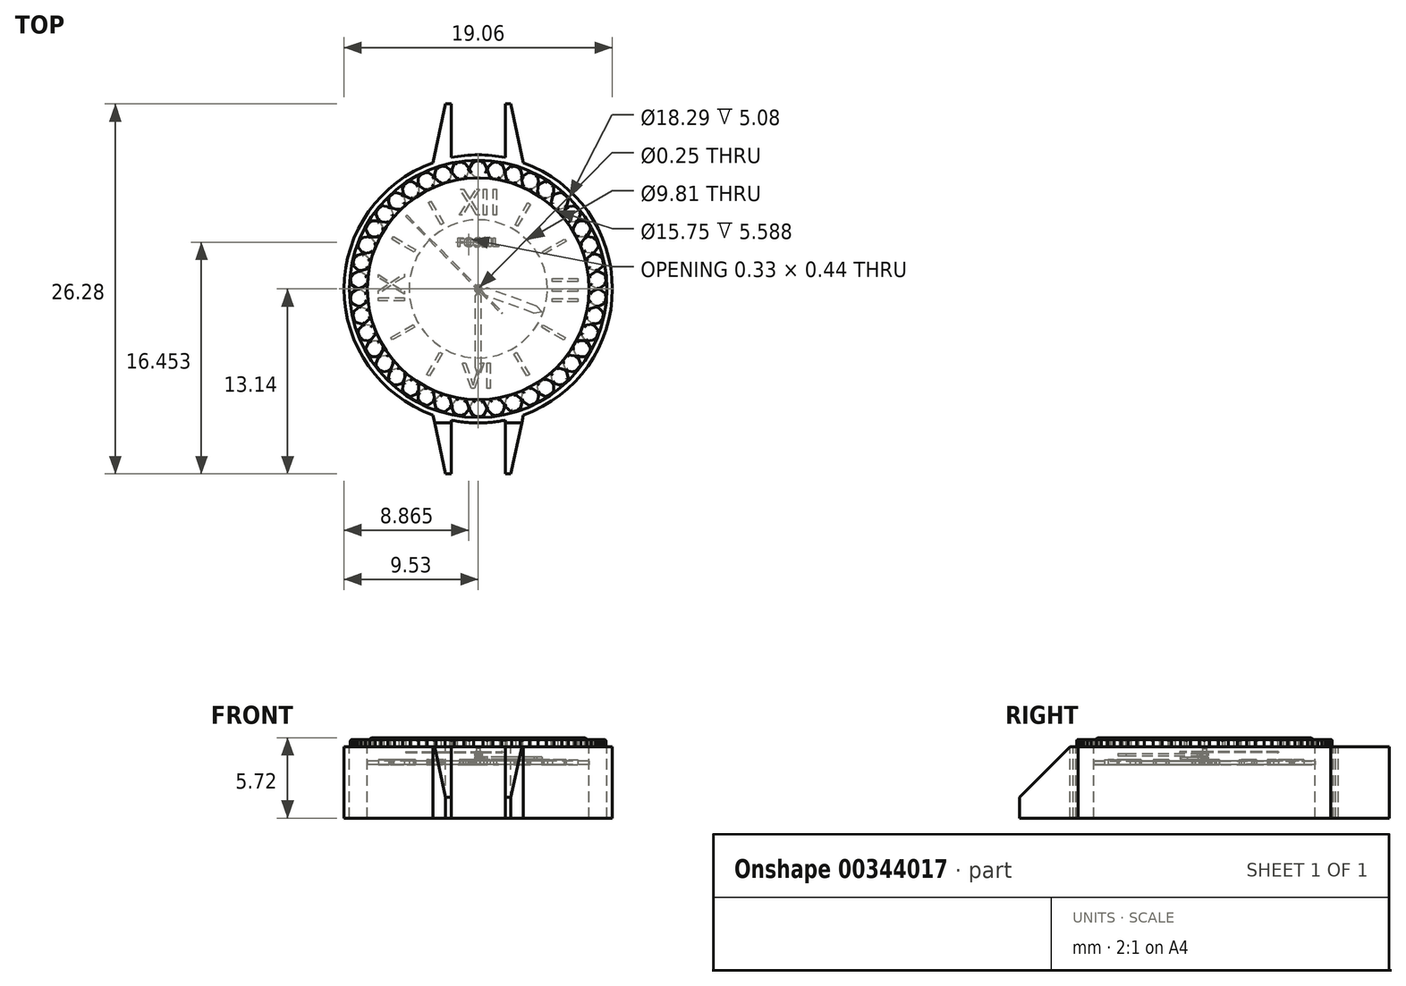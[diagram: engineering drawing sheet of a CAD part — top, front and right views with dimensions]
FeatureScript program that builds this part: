
annotation { "Feature Type Name" : "Feature", "Feature Type Description" : "" }
export const myFeature = defineFeature(function(context is Context, id is Id, definition is map)
    precondition{}
    {
        {
            var Q0;
            Q0=qCreatedBy(makeId("Top.planeOp"),FACE);
            var sketch = newSketch(context, id + "F0", { "sketchPlane" : qUnion([Q0])});
            skCircle(sketch, "E0", {"center": v(0, 0) * mm, "radius": 7.87 * mm});
            skCircle(sketch, "E1", {"center": v(0, 0) * mm, "radius": 9.14 * mm});
            skArc(sketch, "E2", {"start": v(1.93, 9.33) * mm, "mid": v(0, 9.53) * mm, "end": v(-1.93, 9.33) * mm});
            skLineSegment(sketch, "E3", {"start": v(3.22, 8.97) * mm, "end": v(2.32, 13.14) * mm});
            skLineSegment(sketch, "E4", {"start": v(1.93, 13.14) * mm, "end": v(1.93, 9.33) * mm});
            skLineSegment(sketch, "E5.MirrorCS", {"start": v(1.93, -13.14) * mm, "end": v(1.93, -9.33) * mm});
            skLineSegment(sketch, "E6.MirrorCS", {"start": v(3.22, -8.97) * mm, "end": v(2.32, -13.14) * mm});
            skLineSegment(sketch, "E7.MirrorCS", {"start": v(-1.93, 13.14) * mm, "end": v(-1.93, 9.33) * mm});
            skLineSegment(sketch, "E8.MirrorCS", {"start": v(-3.22, 8.97) * mm, "end": v(-2.32, 13.14) * mm});
            skLineSegment(sketch, "E9.MirrorCS", {"start": v(-3.22, -8.97) * mm, "end": v(-2.32, -13.14) * mm});
            skLineSegment(sketch, "E10.MirrorCS", {"start": v(-1.93, -13.14) * mm, "end": v(-1.93, -9.33) * mm});
            skArc(sketch, "E11.trimOffspring", {"start": v(-3.22, 8.97) * mm, "mid": v(-9.52, 0) * mm, "end": v(-3.22, -8.97) * mm});
            skArc(sketch, "E12.trimOffspring", {"start": v(3.22, -8.97) * mm, "mid": v(9.53, 0) * mm, "end": v(3.22, 8.97) * mm});
            skArc(sketch, "E13.trimOffspring", {"start": v(-1.93, -9.33) * mm, "mid": v(0, -9.53) * mm, "end": v(1.93, -9.33) * mm});
            skLineSegment(sketch, "E14", {"start": v(2.32, 13.14) * mm, "end": v(1.93, 13.14) * mm});
            skLineSegment(sketch, "E15.MirrorCS", {"start": v(-2.32, 13.14) * mm, "end": v(-1.93, 13.14) * mm});
            skLineSegment(sketch, "E16.MirrorCS", {"start": v(2.32, -13.14) * mm, "end": v(1.93, -13.14) * mm});
            skLineSegment(sketch, "E17.MirrorCS", {"start": v(-2.32, -13.14) * mm, "end": v(-1.93, -13.14) * mm});
            skLineSegment(sketch, "E18", {"start": v(0, 7.87) * mm, "end": v(0, -7.87) * mm, "construction": true});
            skSolve(sketch);
        }
        {
            var Q0;
            Q0=makeQuery(id+"F0.imprint","IMPRINT",FACE,{"disambiguationData":[TD([[makeQuery(id+"F0.imprint","IMPRINT",EDGE,{"derivedFrom":sQuery(id+"F0.wireOp",EDGE,"E1")}),-1.0]])]});
            var Q1;
            Q1=sQuery(id+"F0.wireOp",EDGE,"E12.trimOffspring");
            var Q2;
            Q2=sQuery(id+"F0.wireOp",EDGE,"E6.MirrorCS");
            var Q3;
            Q3=sQuery(id+"F0.wireOp",EDGE,"E5.MirrorCS");
            var Q4;
            Q4=sQuery(id+"F0.wireOp",EDGE,"E13.trimOffspring");
            var Q5;
            Q5=sQuery(id+"F0.wireOp",EDGE,"E10.MirrorCS");
            var Q6;
            Q6=sQuery(id+"F0.wireOp",EDGE,"E17.MirrorCS");
            var Q7;
            Q7=sQuery(id+"F0.wireOp",EDGE,"E9.MirrorCS");
            var Q8;
            Q8=sQuery(id+"F0.wireOp",EDGE,"E11.trimOffspring");
            extrude(context, id + "F1", {"entities" : qUnion([Q0]), "surfaceEntities" : qUnion([Q1, Q2, Q3, Q4, Q5, Q6, Q7, Q8]), "oppositeDirection" : true, "depth" : 5.08 * mm});
        }
        {
            var Q0;
            Q0=qCreatedBy(makeId("Top.planeOp"),FACE);
            cPlane(context, id + "F2", {"entities" : qUnion([Q0]), "cplaneType" : CPlaneType.OFFSET, "offset" : 1.27 * mm, "oppositeDirection" : true, "width" : 152.4 * mm, "height" : 152.4 * mm});
        }
        {
            var Q0;
            Q0=qCreatedBy(id+"F2.planeOp",FACE);
            var sketch = newSketch(context, id + "F3", { "sketchPlane" : qUnion([Q0])});
            skCircle(sketch, "E19", {"center": v(0.05, 0) * mm, "radius": 7.87 * mm, "construction": true});
            skLineSegment(sketch, "E20", {"start": v(0.05, 7.09) * mm, "end": v(0.05, 0) * mm, "construction": true});
            skText(sketch, "E21", { "text": "XII", "fontName": "OpenSans-Regular.ttf"});
            skLineSegment(sketch, "E22.1.0", {"start": v(-3.5, 6.16) * mm, "end": v(0.05, 0.03) * mm, "construction": true});
            skLineSegment(sketch, "E22.2.0", {"start": v(-6.1, 3.59) * mm, "end": v(0.03, 0.05) * mm, "construction": true});
            skLineSegment(sketch, "E22.3.0", {"start": v(-7.09, 0.05) * mm, "end": v(0, 0.05) * mm, "construction": true});
            skLineSegment(sketch, "E22.4.0", {"start": v(-6.16, -3.5) * mm, "end": v(-0.03, 0.05) * mm, "construction": true});
            skLineSegment(sketch, "E22.5.0", {"start": v(-3.59, -6.1) * mm, "end": v(-0.05, 0.03) * mm, "construction": true});
            skLineSegment(sketch, "E22.6.0", {"start": v(-0.05, -7.09) * mm, "end": v(-0.05, 0) * mm, "construction": true});
            skLineSegment(sketch, "E22.7.0", {"start": v(3.5, -6.16) * mm, "end": v(-0.05, -0.03) * mm, "construction": true});
            skLineSegment(sketch, "E22.8.0", {"start": v(6.1, -3.59) * mm, "end": v(-0.03, -0.05) * mm, "construction": true});
            skLineSegment(sketch, "E22.9.0", {"start": v(7.09, -0.05) * mm, "end": v(0, -0.05) * mm, "construction": true});
            skLineSegment(sketch, "E22.10.0", {"start": v(6.16, 3.5) * mm, "end": v(0.03, -0.05) * mm, "construction": true});
            skLineSegment(sketch, "E22.11.0", {"start": v(3.59, 6.1) * mm, "end": v(0.05, -0.03) * mm, "construction": true});
            skPoint(sketch, "E22.center", {"position": v(0, 0) * mm});
            skText(sketch, "E23", { "text": "I", "fontName": "OpenSans-Regular.ttf"});
            skText(sketch, "E24", { "text": "III", "fontName": "OpenSans-Regular.ttf"});
            skText(sketch, "E25", { "text": "I", "fontName": "OpenSans-Regular.ttf"});
            skText(sketch, "E26", { "text": "I", "fontName": "OpenSans-Regular.ttf"});
            skText(sketch, "E27", { "text": "I", "fontName": "OpenSans-Regular.ttf"});
            skText(sketch, "E28", { "text": "VI", "fontName": "OpenSans-Regular.ttf"});
            skText(sketch, "E29", { "text": "I", "fontName": "OpenSans-Regular.ttf"});
            skText(sketch, "E30", { "text": "I", "fontName": "OpenSans-Regular.ttf"});
            skText(sketch, "E31", { "text": "IX", "fontName": "OpenSans-Regular.ttf"});
            skText(sketch, "E32", { "text": "I", "fontName": "OpenSans-Regular.ttf"});
            skText(sketch, "E33", { "text": "I", "fontName": "OpenSans-Regular.ttf"});
            skPoint(sketch, "E33.secondSnap0", {"position": v(-1.67, 5.13) * mm});
            const initialGuessF3  = {"E21": [-0.00134, 0.00526, 1, 0, 0.00183], "E23": [0.0024, 0.00468, 0.86603, -0.5, 0.00183], "E24": [0.00526, 0.00097, 0, -1, 0.00183], "E25": [0.00443, 0.00285, 0.5, -0.86603, 0.00183], "E26": [0.00595, -0.00386, 0.5, 0.86603, 0.00183], "E27": [0.00323, -0.00632, 0.86603, 0.5, 0.00183], "E28": [-0.00112, -0.00709, 1, 0, 0.00183], "E29": [-0.00386, -0.00595, 0.86603, -0.5, 0.00183], "E30": [-0.00632, -0.00323, 0.5, -0.86603, 0.00183], "E31": [-0.00526, -0.0011, 0, 1, 0.00183], "E32": [-0.00468, 0.0024, 0.5, 0.86603, 0.00183], "E33": [-0.00285, 0.00443, 0.86603, 0.5, 0.00183]};
            skSetInitialGuess(sketch, initialGuessF3);
            skSolve(sketch);
        }
        {
            var Q0;
            Q0=qCreatedBy(makeId("Front.planeOp"),FACE);
            var sketch = newSketch(context, id + "F4", { "sketchPlane" : qUnion([Q0])});
            skLineSegment(sketch, "E34", {"start": v(0, 57.98) * mm, "end": v(0, -59.61) * mm, "construction": true});
            skSolve(sketch);
        }
        {
            var Q0;
            Q0 = qSketchRegion(id + "F3", true);
            extrude(context, id + "F5", {"entities" : qUnion([Q0]), "depth" : 0.33 * mm});
        }
        {
            var Q0;
            Q0=makeQuery(id+"F0.imprint","IMPRINT",FACE,{"disambiguationData":[TD([[makeQuery(id+"F0.imprint","IMPRINT",EDGE,{"derivedFrom":sQuery(id+"F0.wireOp",EDGE,"E0")}),1.0]])]});
            var Q1;
            Q1=sQuery(id+"F0.wireOp",EDGE,"E18");
            var Q2;
            Q2=sQuery(id+"F0.wireOp",EDGE,"E0");
            extrude(context, id + "F6", {"entities" : qUnion([Q0]), "surfaceEntities" : qUnion([Q1, Q2]), "depth" : 0.64 * mm});
        }
        {
            var Q0;
            Q0=makeQuery(id+"F6.opExtrude","CAP_FACE",FACE,{"disambiguationData":[OSD([sQuery(id+"F0.wireOp",EDGE,"E0")])],"isStart":false});
            fillet(context, id + "F7", {"entities" : qUnion([Q0]), "radius" : 0.43 * mm, "tangentPropagation" : true, "allowEdgeOverflow" : false});
        }
        {
            var Q0;
            Q0=makeQuery(id+"F0.imprint","IMPRINT",FACE,{"disambiguationData":[TD([[makeQuery(id+"F0.imprint","IMPRINT",EDGE,{"derivedFrom":sQuery(id+"F0.wireOp",EDGE,"E0")}),-1.0]])]});
            var Q1;
            Q1=makeQuery(id+"F1.opExtrude","CAP_FACE",FACE,{"disambiguationData":[OSD([sQuery(id+"F0.wireOp",EDGE,"E1"),sQuery(id+"F0.wireOp",EDGE,"E2"),sQuery(id+"F0.wireOp",EDGE,"E3"),sQuery(id+"F0.wireOp",EDGE,"E4"),sQuery(id+"F0.wireOp",EDGE,"E5.MirrorCS"),sQuery(id+"F0.wireOp",EDGE,"E6.MirrorCS"),sQuery(id+"F0.wireOp",EDGE,"E7.MirrorCS"),sQuery(id+"F0.wireOp",EDGE,"E8.MirrorCS"),sQuery(id+"F0.wireOp",EDGE,"E9.MirrorCS"),sQuery(id+"F0.wireOp",EDGE,"E10.MirrorCS"),sQuery(id+"F0.wireOp",EDGE,"E11.trimOffspring"),sQuery(id+"F0.wireOp",EDGE,"E12.trimOffspring"),sQuery(id+"F0.wireOp",EDGE,"E13.trimOffspring"),sQuery(id+"F0.wireOp",EDGE,"E14"),sQuery(id+"F0.wireOp",EDGE,"E15.MirrorCS"),sQuery(id+"F0.wireOp",EDGE,"E16.MirrorCS"),sQuery(id+"F0.wireOp",EDGE,"E17.MirrorCS")])],"isStart":false});
            extrude(context, id + "F8", {"entities" : qUnion([Q0]), "endBound" : BoundingType.UP_TO_SURFACE, "oppositeDirection" : true, "endBoundEntityFace" : qUnion([Q1]), "depth" : 25.4 * mm, "hasSecondDirection" : true, "secondDirectionOppositeDirection" : false, "secondDirectionDepth" : 0.5 * mm});
        }
        {
            var Q0;
            Q0=makeQuery(id+"F0.imprint","IMPRINT",FACE,{"disambiguationData":[TD([[makeQuery(id+"F0.imprint","IMPRINT",EDGE,{"derivedFrom":sQuery(id+"F0.wireOp",EDGE,"E0")}),-1.0]])]});
            var sketch = newSketch(context, id + "F9", { "sketchPlane" : qUnion([Q0])});
            skCircle(sketch, "E35.cCircle", {"center": v(0, 8.5) * mm, "radius": 0.57 * mm});
            skLineSegment(sketch, "E35.0", {"start": v(0.65, 8.5) * mm, "end": v(0.33, 7.94) * mm});
            skLineSegment(sketch, "E35.1", {"start": v(0.33, 7.94) * mm, "end": v(-0.33, 7.94) * mm});
            skLineSegment(sketch, "E35.2", {"start": v(-0.33, 7.94) * mm, "end": v(-0.65, 8.5) * mm});
            skLineSegment(sketch, "E35.3", {"start": v(-0.65, 8.5) * mm, "end": v(-0.33, 9.08) * mm});
            skLineSegment(sketch, "E35.4", {"start": v(-0.33, 9.08) * mm, "end": v(0.33, 9.08) * mm});
            skLineSegment(sketch, "E35.5", {"start": v(0.33, 9.08) * mm, "end": v(0.65, 8.5) * mm});
            skPoint(sketch, "E35.0.midPoint", {"position": v(0.5, 8.23) * mm});
            skPoint(sketch, "E36.center", {"position": v(0, 0) * mm});
            skLineSegment(sketch, "E37.1.0", {"start": v(-1.68, 8.93) * mm, "end": v(-1.03, 9.02) * mm});
            skLineSegment(sketch, "E37.1.1", {"start": v(-1.03, 9.02) * mm, "end": v(-0.62, 8.51) * mm});
            skLineSegment(sketch, "E37.1.2", {"start": v(-0.62, 8.51) * mm, "end": v(-0.86, 7.9) * mm});
            skLineSegment(sketch, "E37.1.3", {"start": v(-0.86, 7.9) * mm, "end": v(-1.5, 7.8) * mm});
            skLineSegment(sketch, "E37.1.4", {"start": v(-1.5, 7.8) * mm, "end": v(-1.91, 8.32) * mm});
            skLineSegment(sketch, "E37.1.5", {"start": v(-1.91, 8.32) * mm, "end": v(-1.68, 8.93) * mm});
            skLineSegment(sketch, "E37.2.0", {"start": v(-2.99, 8.58) * mm, "end": v(-2.36, 8.77) * mm});
            skLineSegment(sketch, "E37.2.1", {"start": v(-2.36, 8.77) * mm, "end": v(-1.88, 8.32) * mm});
            skLineSegment(sketch, "E37.2.2", {"start": v(-1.88, 8.32) * mm, "end": v(-2.03, 7.69) * mm});
            skLineSegment(sketch, "E37.2.3", {"start": v(-2.03, 7.69) * mm, "end": v(-2.65, 7.5) * mm});
            skLineSegment(sketch, "E37.2.4", {"start": v(-2.65, 7.5) * mm, "end": v(-3.13, 7.94) * mm});
            skLineSegment(sketch, "E37.2.5", {"start": v(-3.13, 7.94) * mm, "end": v(-2.99, 8.58) * mm});
            skLineSegment(sketch, "E37.3.0", {"start": v(-4.23, 8.03) * mm, "end": v(-3.64, 8.32) * mm});
            skLineSegment(sketch, "E37.3.1", {"start": v(-3.64, 8.32) * mm, "end": v(-3.1, 7.95) * mm});
            skLineSegment(sketch, "E37.3.2", {"start": v(-3.1, 7.95) * mm, "end": v(-3.15, 7.3) * mm});
            skLineSegment(sketch, "E37.3.3", {"start": v(-3.15, 7.3) * mm, "end": v(-3.74, 7.01) * mm});
            skLineSegment(sketch, "E37.3.4", {"start": v(-3.74, 7.01) * mm, "end": v(-4.28, 7.38) * mm});
            skLineSegment(sketch, "E37.3.5", {"start": v(-4.28, 7.38) * mm, "end": v(-4.23, 8.03) * mm});
            skLineSegment(sketch, "E37.4.0", {"start": v(-5.38, 7.31) * mm, "end": v(-4.84, 7.68) * mm});
            skLineSegment(sketch, "E37.4.1", {"start": v(-4.84, 7.68) * mm, "end": v(-4.25, 7.4) * mm});
            skLineSegment(sketch, "E37.4.2", {"start": v(-4.25, 7.4) * mm, "end": v(-4.2, 6.75) * mm});
            skLineSegment(sketch, "E37.4.3", {"start": v(-4.2, 6.75) * mm, "end": v(-4.74, 6.38) * mm});
            skLineSegment(sketch, "E37.4.4", {"start": v(-4.74, 6.38) * mm, "end": v(-5.33, 6.66) * mm});
            skLineSegment(sketch, "E37.4.5", {"start": v(-5.33, 6.66) * mm, "end": v(-5.38, 7.31) * mm});
            skLineSegment(sketch, "E37.5.0", {"start": v(-6.41, 6.43) * mm, "end": v(-5.93, 6.88) * mm});
            skLineSegment(sketch, "E37.5.1", {"start": v(-5.93, 6.88) * mm, "end": v(-5.3, 6.68) * mm});
            skLineSegment(sketch, "E37.5.2", {"start": v(-5.3, 6.68) * mm, "end": v(-5.16, 6.04) * mm});
            skLineSegment(sketch, "E37.5.3", {"start": v(-5.16, 6.04) * mm, "end": v(-5.64, 5.6) * mm});
            skLineSegment(sketch, "E37.5.4", {"start": v(-5.64, 5.6) * mm, "end": v(-6.27, 5.8) * mm});
            skLineSegment(sketch, "E37.5.5", {"start": v(-6.27, 5.8) * mm, "end": v(-6.41, 6.43) * mm});
            skLineSegment(sketch, "E37.6.0", {"start": v(-7.3, 5.4) * mm, "end": v(-6.9, 5.91) * mm});
            skLineSegment(sketch, "E37.6.1", {"start": v(-6.9, 5.91) * mm, "end": v(-6.24, 5.82) * mm});
            skLineSegment(sketch, "E37.6.2", {"start": v(-6.24, 5.82) * mm, "end": v(-6, 5.2) * mm});
            skLineSegment(sketch, "E37.6.3", {"start": v(-6, 5.2) * mm, "end": v(-6.41, 4.7) * mm});
            skLineSegment(sketch, "E37.6.4", {"start": v(-6.41, 4.7) * mm, "end": v(-7.06, 4.8) * mm});
            skLineSegment(sketch, "E37.6.5", {"start": v(-7.06, 4.8) * mm, "end": v(-7.3, 5.4) * mm});
            skLineSegment(sketch, "E37.7.0", {"start": v(-8.02, 4.25) * mm, "end": v(-7.7, 4.82) * mm});
            skLineSegment(sketch, "E37.7.1", {"start": v(-7.7, 4.82) * mm, "end": v(-7.04, 4.82) * mm});
            skLineSegment(sketch, "E37.7.2", {"start": v(-7.04, 4.82) * mm, "end": v(-6.71, 4.25) * mm});
            skLineSegment(sketch, "E37.7.3", {"start": v(-6.71, 4.25) * mm, "end": v(-7.04, 3.69) * mm});
            skLineSegment(sketch, "E37.7.4", {"start": v(-7.04, 3.69) * mm, "end": v(-7.7, 3.69) * mm});
            skLineSegment(sketch, "E37.7.5", {"start": v(-7.7, 3.69) * mm, "end": v(-8.02, 4.25) * mm});
            skLineSegment(sketch, "E37.8.0", {"start": v(-8.57, 3.01) * mm, "end": v(-8.33, 3.62) * mm});
            skLineSegment(sketch, "E37.8.1", {"start": v(-8.33, 3.62) * mm, "end": v(-7.68, 3.72) * mm});
            skLineSegment(sketch, "E37.8.2", {"start": v(-7.68, 3.72) * mm, "end": v(-7.27, 3.2) * mm});
            skLineSegment(sketch, "E37.8.3", {"start": v(-7.27, 3.2) * mm, "end": v(-7.51, 2.6) * mm});
            skLineSegment(sketch, "E37.8.4", {"start": v(-7.51, 2.6) * mm, "end": v(-8.16, 2.5) * mm});
            skLineSegment(sketch, "E37.8.5", {"start": v(-8.16, 2.5) * mm, "end": v(-8.57, 3.01) * mm});
            skLineSegment(sketch, "E37.9.0", {"start": v(-8.92, 1.7) * mm, "end": v(-8.77, 2.34) * mm});
            skLineSegment(sketch, "E37.9.1", {"start": v(-8.77, 2.34) * mm, "end": v(-8.15, 2.53) * mm});
            skLineSegment(sketch, "E37.9.2", {"start": v(-8.15, 2.53) * mm, "end": v(-7.67, 2.09) * mm});
            skLineSegment(sketch, "E37.9.3", {"start": v(-7.67, 2.09) * mm, "end": v(-7.82, 1.45) * mm});
            skLineSegment(sketch, "E37.9.4", {"start": v(-7.82, 1.45) * mm, "end": v(-8.44, 1.26) * mm});
            skLineSegment(sketch, "E37.9.5", {"start": v(-8.44, 1.26) * mm, "end": v(-8.92, 1.7) * mm});
            skLineSegment(sketch, "E37.10.0", {"start": v(-9.07, 0.35) * mm, "end": v(-9.03, 1) * mm});
            skLineSegment(sketch, "E37.10.1", {"start": v(-9.03, 1) * mm, "end": v(-8.44, 1.29) * mm});
            skLineSegment(sketch, "E37.10.2", {"start": v(-8.44, 1.29) * mm, "end": v(-7.9, 0.92) * mm});
            skLineSegment(sketch, "E37.10.3", {"start": v(-7.9, 0.92) * mm, "end": v(-7.94, 0.27) * mm});
            skLineSegment(sketch, "E37.10.4", {"start": v(-7.94, 0.27) * mm, "end": v(-8.53, -0.02) * mm});
            skLineSegment(sketch, "E37.10.5", {"start": v(-8.53, -0.02) * mm, "end": v(-9.07, 0.35) * mm});
            skLineSegment(sketch, "E37.11.0", {"start": v(-9.03, -1) * mm, "end": v(-9.07, -0.35) * mm});
            skLineSegment(sketch, "E37.11.1", {"start": v(-9.07, -0.35) * mm, "end": v(-8.53, 0.02) * mm});
            skLineSegment(sketch, "E37.11.2", {"start": v(-8.53, 0.02) * mm, "end": v(-7.94, -0.27) * mm});
            skLineSegment(sketch, "E37.11.3", {"start": v(-7.94, -0.27) * mm, "end": v(-7.9, -0.92) * mm});
            skLineSegment(sketch, "E37.11.4", {"start": v(-7.9, -0.92) * mm, "end": v(-8.44, -1.29) * mm});
            skLineSegment(sketch, "E37.11.5", {"start": v(-8.44, -1.29) * mm, "end": v(-9.03, -1) * mm});
            skLineSegment(sketch, "E37.12.0", {"start": v(-8.77, -2.34) * mm, "end": v(-8.92, -1.7) * mm});
            skLineSegment(sketch, "E37.12.1", {"start": v(-8.92, -1.7) * mm, "end": v(-8.44, -1.26) * mm});
            skLineSegment(sketch, "E37.12.2", {"start": v(-8.44, -1.26) * mm, "end": v(-7.82, -1.45) * mm});
            skLineSegment(sketch, "E37.12.3", {"start": v(-7.82, -1.45) * mm, "end": v(-7.67, -2.09) * mm});
            skLineSegment(sketch, "E37.12.4", {"start": v(-7.67, -2.09) * mm, "end": v(-8.15, -2.53) * mm});
            skLineSegment(sketch, "E37.12.5", {"start": v(-8.15, -2.53) * mm, "end": v(-8.77, -2.34) * mm});
            skLineSegment(sketch, "E37.13.0", {"start": v(-8.33, -3.62) * mm, "end": v(-8.57, -3.01) * mm});
            skLineSegment(sketch, "E37.13.1", {"start": v(-8.57, -3.01) * mm, "end": v(-8.16, -2.5) * mm});
            skLineSegment(sketch, "E37.13.2", {"start": v(-8.16, -2.5) * mm, "end": v(-7.51, -2.6) * mm});
            skLineSegment(sketch, "E37.13.3", {"start": v(-7.51, -2.6) * mm, "end": v(-7.27, -3.2) * mm});
            skLineSegment(sketch, "E37.13.4", {"start": v(-7.27, -3.2) * mm, "end": v(-7.68, -3.72) * mm});
            skLineSegment(sketch, "E37.13.5", {"start": v(-7.68, -3.72) * mm, "end": v(-8.33, -3.62) * mm});
            skLineSegment(sketch, "E37.14.0", {"start": v(-7.7, -4.82) * mm, "end": v(-8.02, -4.25) * mm});
            skLineSegment(sketch, "E37.14.1", {"start": v(-8.02, -4.25) * mm, "end": v(-7.7, -3.69) * mm});
            skLineSegment(sketch, "E37.14.2", {"start": v(-7.7, -3.69) * mm, "end": v(-7.04, -3.69) * mm});
            skLineSegment(sketch, "E37.14.3", {"start": v(-7.04, -3.69) * mm, "end": v(-6.71, -4.25) * mm});
            skLineSegment(sketch, "E37.14.4", {"start": v(-6.71, -4.25) * mm, "end": v(-7.04, -4.82) * mm});
            skLineSegment(sketch, "E37.14.5", {"start": v(-7.04, -4.82) * mm, "end": v(-7.7, -4.82) * mm});
            skLineSegment(sketch, "E37.15.0", {"start": v(-6.9, -5.91) * mm, "end": v(-7.3, -5.4) * mm});
            skLineSegment(sketch, "E37.15.1", {"start": v(-7.3, -5.4) * mm, "end": v(-7.06, -4.8) * mm});
            skLineSegment(sketch, "E37.15.2", {"start": v(-7.06, -4.8) * mm, "end": v(-6.41, -4.7) * mm});
            skLineSegment(sketch, "E37.15.3", {"start": v(-6.41, -4.7) * mm, "end": v(-6, -5.2) * mm});
            skLineSegment(sketch, "E37.15.4", {"start": v(-6, -5.2) * mm, "end": v(-6.24, -5.82) * mm});
            skLineSegment(sketch, "E37.15.5", {"start": v(-6.24, -5.82) * mm, "end": v(-6.9, -5.91) * mm});
            skLineSegment(sketch, "E37.16.0", {"start": v(-5.93, -6.88) * mm, "end": v(-6.41, -6.43) * mm});
            skLineSegment(sketch, "E37.16.1", {"start": v(-6.41, -6.43) * mm, "end": v(-6.27, -5.8) * mm});
            skLineSegment(sketch, "E37.16.2", {"start": v(-6.27, -5.8) * mm, "end": v(-5.64, -5.6) * mm});
            skLineSegment(sketch, "E37.16.3", {"start": v(-5.64, -5.6) * mm, "end": v(-5.16, -6.04) * mm});
            skLineSegment(sketch, "E37.16.4", {"start": v(-5.16, -6.04) * mm, "end": v(-5.3, -6.68) * mm});
            skLineSegment(sketch, "E37.16.5", {"start": v(-5.3, -6.68) * mm, "end": v(-5.93, -6.88) * mm});
            skLineSegment(sketch, "E37.17.0", {"start": v(-4.84, -7.68) * mm, "end": v(-5.38, -7.31) * mm});
            skLineSegment(sketch, "E37.17.1", {"start": v(-5.38, -7.31) * mm, "end": v(-5.33, -6.66) * mm});
            skLineSegment(sketch, "E37.17.2", {"start": v(-5.33, -6.66) * mm, "end": v(-4.74, -6.38) * mm});
            skLineSegment(sketch, "E37.17.3", {"start": v(-4.74, -6.38) * mm, "end": v(-4.2, -6.75) * mm});
            skLineSegment(sketch, "E37.17.4", {"start": v(-4.2, -6.75) * mm, "end": v(-4.25, -7.4) * mm});
            skLineSegment(sketch, "E37.17.5", {"start": v(-4.25, -7.4) * mm, "end": v(-4.84, -7.68) * mm});
            skLineSegment(sketch, "E37.18.0", {"start": v(-3.64, -8.32) * mm, "end": v(-4.23, -8.03) * mm});
            skLineSegment(sketch, "E37.18.1", {"start": v(-4.23, -8.03) * mm, "end": v(-4.28, -7.38) * mm});
            skLineSegment(sketch, "E37.18.2", {"start": v(-4.28, -7.38) * mm, "end": v(-3.74, -7.01) * mm});
            skLineSegment(sketch, "E37.18.3", {"start": v(-3.74, -7.01) * mm, "end": v(-3.15, -7.3) * mm});
            skLineSegment(sketch, "E37.18.4", {"start": v(-3.15, -7.3) * mm, "end": v(-3.1, -7.95) * mm});
            skLineSegment(sketch, "E37.18.5", {"start": v(-3.1, -7.95) * mm, "end": v(-3.64, -8.32) * mm});
            skLineSegment(sketch, "E37.19.0", {"start": v(-2.36, -8.77) * mm, "end": v(-2.99, -8.58) * mm});
            skLineSegment(sketch, "E37.19.1", {"start": v(-2.99, -8.58) * mm, "end": v(-3.13, -7.94) * mm});
            skLineSegment(sketch, "E37.19.2", {"start": v(-3.13, -7.94) * mm, "end": v(-2.65, -7.5) * mm});
            skLineSegment(sketch, "E37.19.3", {"start": v(-2.65, -7.5) * mm, "end": v(-2.03, -7.69) * mm});
            skLineSegment(sketch, "E37.19.4", {"start": v(-2.03, -7.69) * mm, "end": v(-1.88, -8.32) * mm});
            skLineSegment(sketch, "E37.19.5", {"start": v(-1.88, -8.32) * mm, "end": v(-2.36, -8.77) * mm});
            skLineSegment(sketch, "E37.20.0", {"start": v(-1.03, -9.02) * mm, "end": v(-1.68, -8.93) * mm});
            skLineSegment(sketch, "E37.20.1", {"start": v(-1.68, -8.93) * mm, "end": v(-1.91, -8.32) * mm});
            skLineSegment(sketch, "E37.20.2", {"start": v(-1.91, -8.32) * mm, "end": v(-1.5, -7.8) * mm});
            skLineSegment(sketch, "E37.20.3", {"start": v(-1.5, -7.8) * mm, "end": v(-0.86, -7.9) * mm});
            skLineSegment(sketch, "E37.20.4", {"start": v(-0.86, -7.9) * mm, "end": v(-0.62, -8.51) * mm});
            skLineSegment(sketch, "E37.20.5", {"start": v(-0.62, -8.51) * mm, "end": v(-1.03, -9.02) * mm});
            skLineSegment(sketch, "E37.21.0", {"start": v(0.33, -9.08) * mm, "end": v(-0.33, -9.08) * mm});
            skLineSegment(sketch, "E37.21.1", {"start": v(-0.33, -9.08) * mm, "end": v(-0.65, -8.5) * mm});
            skLineSegment(sketch, "E37.21.2", {"start": v(-0.65, -8.5) * mm, "end": v(-0.33, -7.94) * mm});
            skLineSegment(sketch, "E37.21.3", {"start": v(-0.33, -7.94) * mm, "end": v(0.33, -7.94) * mm});
            skLineSegment(sketch, "E37.21.4", {"start": v(0.33, -7.94) * mm, "end": v(0.65, -8.5) * mm});
            skLineSegment(sketch, "E37.21.5", {"start": v(0.65, -8.5) * mm, "end": v(0.33, -9.08) * mm});
            skLineSegment(sketch, "E37.22.0", {"start": v(1.68, -8.93) * mm, "end": v(1.03, -9.02) * mm});
            skLineSegment(sketch, "E37.22.1", {"start": v(1.03, -9.02) * mm, "end": v(0.62, -8.51) * mm});
            skLineSegment(sketch, "E37.22.2", {"start": v(0.62, -8.51) * mm, "end": v(0.86, -7.9) * mm});
            skLineSegment(sketch, "E37.22.3", {"start": v(0.86, -7.9) * mm, "end": v(1.5, -7.8) * mm});
            skLineSegment(sketch, "E37.22.4", {"start": v(1.5, -7.8) * mm, "end": v(1.91, -8.32) * mm});
            skLineSegment(sketch, "E37.22.5", {"start": v(1.91, -8.32) * mm, "end": v(1.68, -8.93) * mm});
            skLineSegment(sketch, "E37.23.0", {"start": v(2.99, -8.58) * mm, "end": v(2.36, -8.77) * mm});
            skLineSegment(sketch, "E37.23.1", {"start": v(2.36, -8.77) * mm, "end": v(1.88, -8.32) * mm});
            skLineSegment(sketch, "E37.23.2", {"start": v(1.88, -8.32) * mm, "end": v(2.03, -7.69) * mm});
            skLineSegment(sketch, "E37.23.3", {"start": v(2.03, -7.69) * mm, "end": v(2.65, -7.5) * mm});
            skLineSegment(sketch, "E37.23.4", {"start": v(2.65, -7.5) * mm, "end": v(3.13, -7.94) * mm});
            skLineSegment(sketch, "E37.23.5", {"start": v(3.13, -7.94) * mm, "end": v(2.99, -8.58) * mm});
            skLineSegment(sketch, "E37.24.0", {"start": v(4.23, -8.03) * mm, "end": v(3.64, -8.32) * mm});
            skLineSegment(sketch, "E37.24.1", {"start": v(3.64, -8.32) * mm, "end": v(3.1, -7.95) * mm});
            skLineSegment(sketch, "E37.24.2", {"start": v(3.1, -7.95) * mm, "end": v(3.15, -7.3) * mm});
            skLineSegment(sketch, "E37.24.3", {"start": v(3.15, -7.3) * mm, "end": v(3.74, -7.01) * mm});
            skLineSegment(sketch, "E37.24.4", {"start": v(3.74, -7.01) * mm, "end": v(4.28, -7.38) * mm});
            skLineSegment(sketch, "E37.24.5", {"start": v(4.28, -7.38) * mm, "end": v(4.23, -8.03) * mm});
            skLineSegment(sketch, "E37.25.0", {"start": v(5.38, -7.31) * mm, "end": v(4.84, -7.68) * mm});
            skLineSegment(sketch, "E37.25.1", {"start": v(4.84, -7.68) * mm, "end": v(4.25, -7.4) * mm});
            skLineSegment(sketch, "E37.25.2", {"start": v(4.25, -7.4) * mm, "end": v(4.2, -6.75) * mm});
            skLineSegment(sketch, "E37.25.3", {"start": v(4.2, -6.75) * mm, "end": v(4.74, -6.38) * mm});
            skLineSegment(sketch, "E37.25.4", {"start": v(4.74, -6.38) * mm, "end": v(5.33, -6.66) * mm});
            skLineSegment(sketch, "E37.25.5", {"start": v(5.33, -6.66) * mm, "end": v(5.38, -7.31) * mm});
            skLineSegment(sketch, "E37.26.0", {"start": v(6.41, -6.43) * mm, "end": v(5.93, -6.88) * mm});
            skLineSegment(sketch, "E37.26.1", {"start": v(5.93, -6.88) * mm, "end": v(5.3, -6.68) * mm});
            skLineSegment(sketch, "E37.26.2", {"start": v(5.3, -6.68) * mm, "end": v(5.16, -6.04) * mm});
            skLineSegment(sketch, "E37.26.3", {"start": v(5.16, -6.04) * mm, "end": v(5.64, -5.6) * mm});
            skLineSegment(sketch, "E37.26.4", {"start": v(5.64, -5.6) * mm, "end": v(6.27, -5.8) * mm});
            skLineSegment(sketch, "E37.26.5", {"start": v(6.27, -5.8) * mm, "end": v(6.41, -6.43) * mm});
            skLineSegment(sketch, "E37.27.0", {"start": v(7.3, -5.4) * mm, "end": v(6.9, -5.91) * mm});
            skLineSegment(sketch, "E37.27.1", {"start": v(6.9, -5.91) * mm, "end": v(6.24, -5.82) * mm});
            skLineSegment(sketch, "E37.27.2", {"start": v(6.24, -5.82) * mm, "end": v(6, -5.2) * mm});
            skLineSegment(sketch, "E37.27.3", {"start": v(6, -5.2) * mm, "end": v(6.41, -4.7) * mm});
            skLineSegment(sketch, "E37.27.4", {"start": v(6.41, -4.7) * mm, "end": v(7.06, -4.8) * mm});
            skLineSegment(sketch, "E37.27.5", {"start": v(7.06, -4.8) * mm, "end": v(7.3, -5.4) * mm});
            skLineSegment(sketch, "E37.28.0", {"start": v(8.02, -4.25) * mm, "end": v(7.7, -4.82) * mm});
            skLineSegment(sketch, "E37.28.1", {"start": v(7.7, -4.82) * mm, "end": v(7.04, -4.82) * mm});
            skLineSegment(sketch, "E37.28.2", {"start": v(7.04, -4.82) * mm, "end": v(6.71, -4.25) * mm});
            skLineSegment(sketch, "E37.28.3", {"start": v(6.71, -4.25) * mm, "end": v(7.04, -3.69) * mm});
            skLineSegment(sketch, "E37.28.4", {"start": v(7.04, -3.69) * mm, "end": v(7.7, -3.69) * mm});
            skLineSegment(sketch, "E37.28.5", {"start": v(7.7, -3.69) * mm, "end": v(8.02, -4.25) * mm});
            skLineSegment(sketch, "E37.29.0", {"start": v(8.57, -3.01) * mm, "end": v(8.33, -3.62) * mm});
            skLineSegment(sketch, "E37.29.1", {"start": v(8.33, -3.62) * mm, "end": v(7.68, -3.72) * mm});
            skLineSegment(sketch, "E37.29.2", {"start": v(7.68, -3.72) * mm, "end": v(7.27, -3.2) * mm});
            skLineSegment(sketch, "E37.29.3", {"start": v(7.27, -3.2) * mm, "end": v(7.51, -2.6) * mm});
            skLineSegment(sketch, "E37.29.4", {"start": v(7.51, -2.6) * mm, "end": v(8.16, -2.5) * mm});
            skLineSegment(sketch, "E37.29.5", {"start": v(8.16, -2.5) * mm, "end": v(8.57, -3.01) * mm});
            skLineSegment(sketch, "E37.30.0", {"start": v(8.92, -1.7) * mm, "end": v(8.77, -2.34) * mm});
            skLineSegment(sketch, "E37.30.1", {"start": v(8.77, -2.34) * mm, "end": v(8.15, -2.53) * mm});
            skLineSegment(sketch, "E37.30.2", {"start": v(8.15, -2.53) * mm, "end": v(7.67, -2.09) * mm});
            skLineSegment(sketch, "E37.30.3", {"start": v(7.67, -2.09) * mm, "end": v(7.82, -1.45) * mm});
            skLineSegment(sketch, "E37.30.4", {"start": v(7.82, -1.45) * mm, "end": v(8.44, -1.26) * mm});
            skLineSegment(sketch, "E37.30.5", {"start": v(8.44, -1.26) * mm, "end": v(8.92, -1.7) * mm});
            skLineSegment(sketch, "E37.31.0", {"start": v(9.07, -0.35) * mm, "end": v(9.03, -1) * mm});
            skLineSegment(sketch, "E37.31.1", {"start": v(9.03, -1) * mm, "end": v(8.44, -1.29) * mm});
            skLineSegment(sketch, "E37.31.2", {"start": v(8.44, -1.29) * mm, "end": v(7.9, -0.92) * mm});
            skLineSegment(sketch, "E37.31.3", {"start": v(7.9, -0.92) * mm, "end": v(7.94, -0.27) * mm});
            skLineSegment(sketch, "E37.31.4", {"start": v(7.94, -0.27) * mm, "end": v(8.53, 0.02) * mm});
            skLineSegment(sketch, "E37.31.5", {"start": v(8.53, 0.02) * mm, "end": v(9.07, -0.35) * mm});
            skLineSegment(sketch, "E37.32.0", {"start": v(9.03, 1) * mm, "end": v(9.07, 0.35) * mm});
            skLineSegment(sketch, "E37.32.1", {"start": v(9.07, 0.35) * mm, "end": v(8.53, -0.02) * mm});
            skLineSegment(sketch, "E37.32.2", {"start": v(8.53, -0.02) * mm, "end": v(7.94, 0.27) * mm});
            skLineSegment(sketch, "E37.32.3", {"start": v(7.94, 0.27) * mm, "end": v(7.9, 0.92) * mm});
            skLineSegment(sketch, "E37.32.4", {"start": v(7.9, 0.92) * mm, "end": v(8.44, 1.29) * mm});
            skLineSegment(sketch, "E37.32.5", {"start": v(8.44, 1.29) * mm, "end": v(9.03, 1) * mm});
            skLineSegment(sketch, "E37.33.0", {"start": v(8.77, 2.34) * mm, "end": v(8.92, 1.7) * mm});
            skLineSegment(sketch, "E37.33.1", {"start": v(8.92, 1.7) * mm, "end": v(8.44, 1.26) * mm});
            skLineSegment(sketch, "E37.33.2", {"start": v(8.44, 1.26) * mm, "end": v(7.82, 1.45) * mm});
            skLineSegment(sketch, "E37.33.3", {"start": v(7.82, 1.45) * mm, "end": v(7.67, 2.09) * mm});
            skLineSegment(sketch, "E37.33.4", {"start": v(7.67, 2.09) * mm, "end": v(8.15, 2.53) * mm});
            skLineSegment(sketch, "E37.33.5", {"start": v(8.15, 2.53) * mm, "end": v(8.77, 2.34) * mm});
            skLineSegment(sketch, "E37.34.0", {"start": v(8.33, 3.62) * mm, "end": v(8.57, 3.01) * mm});
            skLineSegment(sketch, "E37.34.1", {"start": v(8.57, 3.01) * mm, "end": v(8.16, 2.5) * mm});
            skLineSegment(sketch, "E37.34.2", {"start": v(8.16, 2.5) * mm, "end": v(7.51, 2.6) * mm});
            skLineSegment(sketch, "E37.34.3", {"start": v(7.51, 2.6) * mm, "end": v(7.27, 3.2) * mm});
            skLineSegment(sketch, "E37.34.4", {"start": v(7.27, 3.2) * mm, "end": v(7.68, 3.72) * mm});
            skLineSegment(sketch, "E37.34.5", {"start": v(7.68, 3.72) * mm, "end": v(8.33, 3.62) * mm});
            skLineSegment(sketch, "E37.35.0", {"start": v(7.7, 4.82) * mm, "end": v(8.02, 4.25) * mm});
            skLineSegment(sketch, "E37.35.1", {"start": v(8.02, 4.25) * mm, "end": v(7.7, 3.69) * mm});
            skLineSegment(sketch, "E37.35.2", {"start": v(7.7, 3.69) * mm, "end": v(7.04, 3.69) * mm});
            skLineSegment(sketch, "E37.35.3", {"start": v(7.04, 3.69) * mm, "end": v(6.71, 4.25) * mm});
            skLineSegment(sketch, "E37.35.4", {"start": v(6.71, 4.25) * mm, "end": v(7.04, 4.82) * mm});
            skLineSegment(sketch, "E37.35.5", {"start": v(7.04, 4.82) * mm, "end": v(7.7, 4.82) * mm});
            skLineSegment(sketch, "E37.36.0", {"start": v(6.9, 5.91) * mm, "end": v(7.3, 5.4) * mm});
            skLineSegment(sketch, "E37.36.1", {"start": v(7.3, 5.4) * mm, "end": v(7.06, 4.8) * mm});
            skLineSegment(sketch, "E37.36.2", {"start": v(7.06, 4.8) * mm, "end": v(6.41, 4.7) * mm});
            skLineSegment(sketch, "E37.36.3", {"start": v(6.41, 4.7) * mm, "end": v(6, 5.2) * mm});
            skLineSegment(sketch, "E37.36.4", {"start": v(6, 5.2) * mm, "end": v(6.24, 5.82) * mm});
            skLineSegment(sketch, "E37.36.5", {"start": v(6.24, 5.82) * mm, "end": v(6.9, 5.91) * mm});
            skLineSegment(sketch, "E37.37.0", {"start": v(5.93, 6.88) * mm, "end": v(6.41, 6.43) * mm});
            skLineSegment(sketch, "E37.37.1", {"start": v(6.41, 6.43) * mm, "end": v(6.27, 5.8) * mm});
            skLineSegment(sketch, "E37.37.2", {"start": v(6.27, 5.8) * mm, "end": v(5.64, 5.6) * mm});
            skLineSegment(sketch, "E37.37.3", {"start": v(5.64, 5.6) * mm, "end": v(5.16, 6.04) * mm});
            skLineSegment(sketch, "E37.37.4", {"start": v(5.16, 6.04) * mm, "end": v(5.3, 6.68) * mm});
            skLineSegment(sketch, "E37.37.5", {"start": v(5.3, 6.68) * mm, "end": v(5.93, 6.88) * mm});
            skLineSegment(sketch, "E37.38.0", {"start": v(4.84, 7.68) * mm, "end": v(5.38, 7.31) * mm});
            skLineSegment(sketch, "E37.38.1", {"start": v(5.38, 7.31) * mm, "end": v(5.33, 6.66) * mm});
            skLineSegment(sketch, "E37.38.2", {"start": v(5.33, 6.66) * mm, "end": v(4.74, 6.38) * mm});
            skLineSegment(sketch, "E37.38.3", {"start": v(4.74, 6.38) * mm, "end": v(4.2, 6.75) * mm});
            skLineSegment(sketch, "E37.38.4", {"start": v(4.2, 6.75) * mm, "end": v(4.25, 7.4) * mm});
            skLineSegment(sketch, "E37.38.5", {"start": v(4.25, 7.4) * mm, "end": v(4.84, 7.68) * mm});
            skLineSegment(sketch, "E37.39.0", {"start": v(3.64, 8.32) * mm, "end": v(4.23, 8.03) * mm});
            skLineSegment(sketch, "E37.39.1", {"start": v(4.23, 8.03) * mm, "end": v(4.28, 7.38) * mm});
            skLineSegment(sketch, "E37.39.2", {"start": v(4.28, 7.38) * mm, "end": v(3.74, 7.01) * mm});
            skLineSegment(sketch, "E37.39.3", {"start": v(3.74, 7.01) * mm, "end": v(3.15, 7.3) * mm});
            skLineSegment(sketch, "E37.39.4", {"start": v(3.15, 7.3) * mm, "end": v(3.1, 7.95) * mm});
            skLineSegment(sketch, "E37.39.5", {"start": v(3.1, 7.95) * mm, "end": v(3.64, 8.32) * mm});
            skLineSegment(sketch, "E37.40.0", {"start": v(2.36, 8.77) * mm, "end": v(2.99, 8.58) * mm});
            skLineSegment(sketch, "E37.40.1", {"start": v(2.99, 8.58) * mm, "end": v(3.13, 7.94) * mm});
            skLineSegment(sketch, "E37.40.2", {"start": v(3.13, 7.94) * mm, "end": v(2.65, 7.5) * mm});
            skLineSegment(sketch, "E37.40.3", {"start": v(2.65, 7.5) * mm, "end": v(2.03, 7.69) * mm});
            skLineSegment(sketch, "E37.40.4", {"start": v(2.03, 7.69) * mm, "end": v(1.88, 8.32) * mm});
            skLineSegment(sketch, "E37.40.5", {"start": v(1.88, 8.32) * mm, "end": v(2.36, 8.77) * mm});
            skLineSegment(sketch, "E37.41.0", {"start": v(1.03, 9.02) * mm, "end": v(1.68, 8.93) * mm});
            skLineSegment(sketch, "E37.41.1", {"start": v(1.68, 8.93) * mm, "end": v(1.91, 8.32) * mm});
            skLineSegment(sketch, "E37.41.2", {"start": v(1.91, 8.32) * mm, "end": v(1.5, 7.8) * mm});
            skLineSegment(sketch, "E37.41.3", {"start": v(1.5, 7.8) * mm, "end": v(0.86, 7.9) * mm});
            skLineSegment(sketch, "E37.41.4", {"start": v(0.86, 7.9) * mm, "end": v(0.62, 8.51) * mm});
            skLineSegment(sketch, "E37.41.5", {"start": v(0.62, 8.51) * mm, "end": v(1.03, 9.02) * mm});
            skSolve(sketch);
        }
        {
            var Q0;
            Q0=qCreatedBy(makeId("Right.planeOp"),FACE);
            var sketch = newSketch(context, id + "F10", { "sketchPlane" : qUnion([Q0])});
            skLineSegment(sketch, "E38", {"start": v(-7.87, 0.5) * mm, "end": v(-9.14, 0) * mm});
            skLineSegment(sketch, "E39", {"start": v(-9.14, 0.5) * mm, "end": v(-7.87, 0.5) * mm});
            skPoint(sketch, "E40.0.end.orphan", {"position": v(7.87, 0.5) * mm});
            skPoint(sketch, "E41.0.end.orphan", {"position": v(9.14, 0) * mm});
            skLineSegment(sketch, "E42", {"start": v(-9.14, 0.5) * mm, "end": v(-9.14, 0) * mm});
            skLineSegment(sketch, "E43", {"start": v(0, 3.16) * mm, "end": v(0, -2.04) * mm, "construction": true});
            skSolve(sketch);
        }
        {
            var Q0;
            Q0=makeQuery(id+"F10.imprint","IMPRINT",FACE,{"disambiguationData":[TD([[makeQuery(id+"F10.imprint","IMPRINT",EDGE,{"derivedFrom":sQuery(id+"F10.wireOp",EDGE,"E38")}),-1.0]])]});
            var Q1;
            Q1=sQuery(id+"F4.wireOp",EDGE,"E34");
            revolve(context, id + "F11", {"operationType" : NewBodyOperationType.REMOVE, "entities" : qUnion([Q0]), "axis" : qUnion([Q1]), "revolveType" : RevolveType.FULL});
        }
        {
            var Q0;
            Q0 = qSketchRegion(id + "F9", true);
            extrude(context, id + "F12", {"entities" : qUnion([Q0]), "depth" : 0.5 * mm});
        }
        {
            var Q0;
            Q0=makeQuery(id+"F12.opExtrude","CAP_FACE",FACE,{"disambiguationData":[OSD([sQuery(id+"F9.wireOp",EDGE,"E35.cCircle"),sQuery(id+"F9.wireOp",EDGE,"E35.0"),sQuery(id+"F9.wireOp",EDGE,"E35.2"),sQuery(id+"F9.wireOp",EDGE,"E35.3"),sQuery(id+"F9.wireOp",EDGE,"E35.4"),sQuery(id+"F9.wireOp",EDGE,"E35.5"),sQuery(id+"F9.wireOp",EDGE,"E37.1.0"),sQuery(id+"F9.wireOp",EDGE,"E37.1.1"),sQuery(id+"F9.wireOp",EDGE,"E37.1.2"),sQuery(id+"F9.wireOp",EDGE,"E37.1.3"),sQuery(id+"F9.wireOp",EDGE,"E37.1.4"),sQuery(id+"F9.wireOp",EDGE,"E37.1.5"),sQuery(id+"F9.wireOp",EDGE,"E37.2.0"),sQuery(id+"F9.wireOp",EDGE,"E37.2.1"),sQuery(id+"F9.wireOp",EDGE,"E37.2.2"),sQuery(id+"F9.wireOp",EDGE,"E37.2.3"),sQuery(id+"F9.wireOp",EDGE,"E37.2.4"),sQuery(id+"F9.wireOp",EDGE,"E37.2.5"),sQuery(id+"F9.wireOp",EDGE,"E37.3.0"),sQuery(id+"F9.wireOp",EDGE,"E37.3.1"),sQuery(id+"F9.wireOp",EDGE,"E37.3.2"),sQuery(id+"F9.wireOp",EDGE,"E37.3.3"),sQuery(id+"F9.wireOp",EDGE,"E37.3.4"),sQuery(id+"F9.wireOp",EDGE,"E37.3.5"),sQuery(id+"F9.wireOp",EDGE,"E37.4.0"),sQuery(id+"F9.wireOp",EDGE,"E37.4.1"),sQuery(id+"F9.wireOp",EDGE,"E37.4.2"),sQuery(id+"F9.wireOp",EDGE,"E37.4.3"),sQuery(id+"F9.wireOp",EDGE,"E37.4.4"),sQuery(id+"F9.wireOp",EDGE,"E37.4.5"),sQuery(id+"F9.wireOp",EDGE,"E37.5.0"),sQuery(id+"F9.wireOp",EDGE,"E37.5.1"),sQuery(id+"F9.wireOp",EDGE,"E37.5.2"),sQuery(id+"F9.wireOp",EDGE,"E37.5.3"),sQuery(id+"F9.wireOp",EDGE,"E37.5.4"),sQuery(id+"F9.wireOp",EDGE,"E37.5.5"),sQuery(id+"F9.wireOp",EDGE,"E37.6.0"),sQuery(id+"F9.wireOp",EDGE,"E37.6.1"),sQuery(id+"F9.wireOp",EDGE,"E37.6.2"),sQuery(id+"F9.wireOp",EDGE,"E37.6.3"),sQuery(id+"F9.wireOp",EDGE,"E37.6.4"),sQuery(id+"F9.wireOp",EDGE,"E37.6.5"),sQuery(id+"F9.wireOp",EDGE,"E37.7.0"),sQuery(id+"F9.wireOp",EDGE,"E37.7.1"),sQuery(id+"F9.wireOp",EDGE,"E37.7.2"),sQuery(id+"F9.wireOp",EDGE,"E37.7.3"),sQuery(id+"F9.wireOp",EDGE,"E37.7.4"),sQuery(id+"F9.wireOp",EDGE,"E37.7.5"),sQuery(id+"F9.wireOp",EDGE,"E37.8.0"),sQuery(id+"F9.wireOp",EDGE,"E37.8.1"),sQuery(id+"F9.wireOp",EDGE,"E37.8.2"),sQuery(id+"F9.wireOp",EDGE,"E37.8.3"),sQuery(id+"F9.wireOp",EDGE,"E37.8.4"),sQuery(id+"F9.wireOp",EDGE,"E37.8.5"),sQuery(id+"F9.wireOp",EDGE,"E37.9.0"),sQuery(id+"F9.wireOp",EDGE,"E37.9.1"),sQuery(id+"F9.wireOp",EDGE,"E37.9.2"),sQuery(id+"F9.wireOp",EDGE,"E37.9.3"),sQuery(id+"F9.wireOp",EDGE,"E37.9.4"),sQuery(id+"F9.wireOp",EDGE,"E37.9.5"),sQuery(id+"F9.wireOp",EDGE,"E37.10.0"),sQuery(id+"F9.wireOp",EDGE,"E37.10.1"),sQuery(id+"F9.wireOp",EDGE,"E37.10.2"),sQuery(id+"F9.wireOp",EDGE,"E37.10.3"),sQuery(id+"F9.wireOp",EDGE,"E37.10.4"),sQuery(id+"F9.wireOp",EDGE,"E37.10.5"),sQuery(id+"F9.wireOp",EDGE,"E37.11.0"),sQuery(id+"F9.wireOp",EDGE,"E37.11.1"),sQuery(id+"F9.wireOp",EDGE,"E37.11.2"),sQuery(id+"F9.wireOp",EDGE,"E37.11.3"),sQuery(id+"F9.wireOp",EDGE,"E37.11.4"),sQuery(id+"F9.wireOp",EDGE,"E37.11.5"),sQuery(id+"F9.wireOp",EDGE,"E37.12.0"),sQuery(id+"F9.wireOp",EDGE,"E37.12.1"),sQuery(id+"F9.wireOp",EDGE,"E37.12.2"),sQuery(id+"F9.wireOp",EDGE,"E37.12.3"),sQuery(id+"F9.wireOp",EDGE,"E37.12.4"),sQuery(id+"F9.wireOp",EDGE,"E37.12.5"),sQuery(id+"F9.wireOp",EDGE,"E37.13.0"),sQuery(id+"F9.wireOp",EDGE,"E37.13.1"),sQuery(id+"F9.wireOp",EDGE,"E37.13.2"),sQuery(id+"F9.wireOp",EDGE,"E37.13.3"),sQuery(id+"F9.wireOp",EDGE,"E37.13.4"),sQuery(id+"F9.wireOp",EDGE,"E37.13.5"),sQuery(id+"F9.wireOp",EDGE,"E37.14.0"),sQuery(id+"F9.wireOp",EDGE,"E37.14.1"),sQuery(id+"F9.wireOp",EDGE,"E37.14.2"),sQuery(id+"F9.wireOp",EDGE,"E37.14.3"),sQuery(id+"F9.wireOp",EDGE,"E37.14.4"),sQuery(id+"F9.wireOp",EDGE,"E37.14.5"),sQuery(id+"F9.wireOp",EDGE,"E37.15.0"),sQuery(id+"F9.wireOp",EDGE,"E37.15.1"),sQuery(id+"F9.wireOp",EDGE,"E37.15.2"),sQuery(id+"F9.wireOp",EDGE,"E37.15.3"),sQuery(id+"F9.wireOp",EDGE,"E37.15.4"),sQuery(id+"F9.wireOp",EDGE,"E37.15.5"),sQuery(id+"F9.wireOp",EDGE,"E37.16.0"),sQuery(id+"F9.wireOp",EDGE,"E37.16.1"),sQuery(id+"F9.wireOp",EDGE,"E37.16.2"),sQuery(id+"F9.wireOp",EDGE,"E37.16.3"),sQuery(id+"F9.wireOp",EDGE,"E37.16.4"),sQuery(id+"F9.wireOp",EDGE,"E37.16.5"),sQuery(id+"F9.wireOp",EDGE,"E37.17.0"),sQuery(id+"F9.wireOp",EDGE,"E37.17.1"),sQuery(id+"F9.wireOp",EDGE,"E37.17.2"),sQuery(id+"F9.wireOp",EDGE,"E37.17.3"),sQuery(id+"F9.wireOp",EDGE,"E37.17.4"),sQuery(id+"F9.wireOp",EDGE,"E37.17.5"),sQuery(id+"F9.wireOp",EDGE,"E37.18.0"),sQuery(id+"F9.wireOp",EDGE,"E37.18.1"),sQuery(id+"F9.wireOp",EDGE,"E37.18.2"),sQuery(id+"F9.wireOp",EDGE,"E37.18.3"),sQuery(id+"F9.wireOp",EDGE,"E37.18.4"),sQuery(id+"F9.wireOp",EDGE,"E37.18.5"),sQuery(id+"F9.wireOp",EDGE,"E37.19.0"),sQuery(id+"F9.wireOp",EDGE,"E37.19.1"),sQuery(id+"F9.wireOp",EDGE,"E37.19.2"),sQuery(id+"F9.wireOp",EDGE,"E37.19.3"),sQuery(id+"F9.wireOp",EDGE,"E37.19.4"),sQuery(id+"F9.wireOp",EDGE,"E37.19.5"),sQuery(id+"F9.wireOp",EDGE,"E37.20.0"),sQuery(id+"F9.wireOp",EDGE,"E37.20.1"),sQuery(id+"F9.wireOp",EDGE,"E37.20.2"),sQuery(id+"F9.wireOp",EDGE,"E37.20.3"),sQuery(id+"F9.wireOp",EDGE,"E37.20.4"),sQuery(id+"F9.wireOp",EDGE,"E37.20.5"),sQuery(id+"F9.wireOp",EDGE,"E37.21.0"),sQuery(id+"F9.wireOp",EDGE,"E37.21.1"),sQuery(id+"F9.wireOp",EDGE,"E37.21.2"),sQuery(id+"F9.wireOp",EDGE,"E37.21.3"),sQuery(id+"F9.wireOp",EDGE,"E37.21.4"),sQuery(id+"F9.wireOp",EDGE,"E37.21.5"),sQuery(id+"F9.wireOp",EDGE,"E37.22.0"),sQuery(id+"F9.wireOp",EDGE,"E37.22.1"),sQuery(id+"F9.wireOp",EDGE,"E37.22.2"),sQuery(id+"F9.wireOp",EDGE,"E37.22.3"),sQuery(id+"F9.wireOp",EDGE,"E37.22.4"),sQuery(id+"F9.wireOp",EDGE,"E37.22.5"),sQuery(id+"F9.wireOp",EDGE,"E37.23.0"),sQuery(id+"F9.wireOp",EDGE,"E37.23.1"),sQuery(id+"F9.wireOp",EDGE,"E37.23.2"),sQuery(id+"F9.wireOp",EDGE,"E37.23.3"),sQuery(id+"F9.wireOp",EDGE,"E37.23.4"),sQuery(id+"F9.wireOp",EDGE,"E37.23.5"),sQuery(id+"F9.wireOp",EDGE,"E37.24.0"),sQuery(id+"F9.wireOp",EDGE,"E37.24.1"),sQuery(id+"F9.wireOp",EDGE,"E37.24.2"),sQuery(id+"F9.wireOp",EDGE,"E37.24.3"),sQuery(id+"F9.wireOp",EDGE,"E37.24.4"),sQuery(id+"F9.wireOp",EDGE,"E37.24.5"),sQuery(id+"F9.wireOp",EDGE,"E37.25.0"),sQuery(id+"F9.wireOp",EDGE,"E37.25.1"),sQuery(id+"F9.wireOp",EDGE,"E37.25.2"),sQuery(id+"F9.wireOp",EDGE,"E37.25.3"),sQuery(id+"F9.wireOp",EDGE,"E37.25.4"),sQuery(id+"F9.wireOp",EDGE,"E37.25.5"),sQuery(id+"F9.wireOp",EDGE,"E37.26.0"),sQuery(id+"F9.wireOp",EDGE,"E37.26.1"),sQuery(id+"F9.wireOp",EDGE,"E37.26.2"),sQuery(id+"F9.wireOp",EDGE,"E37.26.3"),sQuery(id+"F9.wireOp",EDGE,"E37.26.4"),sQuery(id+"F9.wireOp",EDGE,"E37.26.5"),sQuery(id+"F9.wireOp",EDGE,"E37.27.0"),sQuery(id+"F9.wireOp",EDGE,"E37.27.1"),sQuery(id+"F9.wireOp",EDGE,"E37.27.2"),sQuery(id+"F9.wireOp",EDGE,"E37.27.3"),sQuery(id+"F9.wireOp",EDGE,"E37.27.4"),sQuery(id+"F9.wireOp",EDGE,"E37.27.5"),sQuery(id+"F9.wireOp",EDGE,"E37.28.0"),sQuery(id+"F9.wireOp",EDGE,"E37.28.1"),sQuery(id+"F9.wireOp",EDGE,"E37.28.2"),sQuery(id+"F9.wireOp",EDGE,"E37.28.3"),sQuery(id+"F9.wireOp",EDGE,"E37.28.4"),sQuery(id+"F9.wireOp",EDGE,"E37.28.5"),sQuery(id+"F9.wireOp",EDGE,"E37.29.0"),sQuery(id+"F9.wireOp",EDGE,"E37.29.1"),sQuery(id+"F9.wireOp",EDGE,"E37.29.2"),sQuery(id+"F9.wireOp",EDGE,"E37.29.3"),sQuery(id+"F9.wireOp",EDGE,"E37.29.4"),sQuery(id+"F9.wireOp",EDGE,"E37.29.5"),sQuery(id+"F9.wireOp",EDGE,"E37.30.0"),sQuery(id+"F9.wireOp",EDGE,"E37.30.1"),sQuery(id+"F9.wireOp",EDGE,"E37.30.2"),sQuery(id+"F9.wireOp",EDGE,"E37.30.3"),sQuery(id+"F9.wireOp",EDGE,"E37.30.4"),sQuery(id+"F9.wireOp",EDGE,"E37.30.5"),sQuery(id+"F9.wireOp",EDGE,"E37.31.0"),sQuery(id+"F9.wireOp",EDGE,"E37.31.1"),sQuery(id+"F9.wireOp",EDGE,"E37.31.2"),sQuery(id+"F9.wireOp",EDGE,"E37.31.3"),sQuery(id+"F9.wireOp",EDGE,"E37.31.4"),sQuery(id+"F9.wireOp",EDGE,"E37.31.5"),sQuery(id+"F9.wireOp",EDGE,"E37.32.0"),sQuery(id+"F9.wireOp",EDGE,"E37.32.1"),sQuery(id+"F9.wireOp",EDGE,"E37.32.2"),sQuery(id+"F9.wireOp",EDGE,"E37.32.3"),sQuery(id+"F9.wireOp",EDGE,"E37.32.4"),sQuery(id+"F9.wireOp",EDGE,"E37.32.5"),sQuery(id+"F9.wireOp",EDGE,"E37.33.0"),sQuery(id+"F9.wireOp",EDGE,"E37.33.1"),sQuery(id+"F9.wireOp",EDGE,"E37.33.2"),sQuery(id+"F9.wireOp",EDGE,"E37.33.3"),sQuery(id+"F9.wireOp",EDGE,"E37.33.4"),sQuery(id+"F9.wireOp",EDGE,"E37.33.5"),sQuery(id+"F9.wireOp",EDGE,"E37.34.0"),sQuery(id+"F9.wireOp",EDGE,"E37.34.1"),sQuery(id+"F9.wireOp",EDGE,"E37.34.2"),sQuery(id+"F9.wireOp",EDGE,"E37.34.3"),sQuery(id+"F9.wireOp",EDGE,"E37.34.4"),sQuery(id+"F9.wireOp",EDGE,"E37.34.5"),sQuery(id+"F9.wireOp",EDGE,"E37.35.0"),sQuery(id+"F9.wireOp",EDGE,"E37.35.1"),sQuery(id+"F9.wireOp",EDGE,"E37.35.2"),sQuery(id+"F9.wireOp",EDGE,"E37.35.3"),sQuery(id+"F9.wireOp",EDGE,"E37.35.4"),sQuery(id+"F9.wireOp",EDGE,"E37.35.5"),sQuery(id+"F9.wireOp",EDGE,"E37.36.0"),sQuery(id+"F9.wireOp",EDGE,"E37.36.1"),sQuery(id+"F9.wireOp",EDGE,"E37.36.2"),sQuery(id+"F9.wireOp",EDGE,"E37.36.3"),sQuery(id+"F9.wireOp",EDGE,"E37.36.4"),sQuery(id+"F9.wireOp",EDGE,"E37.36.5"),sQuery(id+"F9.wireOp",EDGE,"E37.37.0"),sQuery(id+"F9.wireOp",EDGE,"E37.37.1"),sQuery(id+"F9.wireOp",EDGE,"E37.37.2"),sQuery(id+"F9.wireOp",EDGE,"E37.37.3"),sQuery(id+"F9.wireOp",EDGE,"E37.37.4"),sQuery(id+"F9.wireOp",EDGE,"E37.37.5"),sQuery(id+"F9.wireOp",EDGE,"E37.38.0"),sQuery(id+"F9.wireOp",EDGE,"E37.38.1"),sQuery(id+"F9.wireOp",EDGE,"E37.38.2"),sQuery(id+"F9.wireOp",EDGE,"E37.38.3"),sQuery(id+"F9.wireOp",EDGE,"E37.38.4"),sQuery(id+"F9.wireOp",EDGE,"E37.38.5"),sQuery(id+"F9.wireOp",EDGE,"E37.39.0"),sQuery(id+"F9.wireOp",EDGE,"E37.39.1"),sQuery(id+"F9.wireOp",EDGE,"E37.39.2"),sQuery(id+"F9.wireOp",EDGE,"E37.39.3"),sQuery(id+"F9.wireOp",EDGE,"E37.39.4"),sQuery(id+"F9.wireOp",EDGE,"E37.39.5"),sQuery(id+"F9.wireOp",EDGE,"E37.40.0"),sQuery(id+"F9.wireOp",EDGE,"E37.40.1"),sQuery(id+"F9.wireOp",EDGE,"E37.40.2"),sQuery(id+"F9.wireOp",EDGE,"E37.40.3"),sQuery(id+"F9.wireOp",EDGE,"E37.40.4"),sQuery(id+"F9.wireOp",EDGE,"E37.40.5"),sQuery(id+"F9.wireOp",EDGE,"E37.41.0"),sQuery(id+"F9.wireOp",EDGE,"E37.41.1"),sQuery(id+"F9.wireOp",EDGE,"E37.41.2"),sQuery(id+"F9.wireOp",EDGE,"E37.41.3"),sQuery(id+"F9.wireOp",EDGE,"E37.41.4"),sQuery(id+"F9.wireOp",EDGE,"E37.41.5")])],"isStart":false});
            fillet(context, id + "F13", {"entities" : qUnion([Q0]), "radius" : 0.13 * mm, "tangentPropagation" : true, "allowEdgeOverflow" : false});
        }
        {
            var Q0;
            Q0=qCreatedBy(id+"F2.planeOp",FACE);
            var sketch = newSketch(context, id + "F14", { "sketchPlane" : qUnion([Q0])});
            skCircle(sketch, "E44", {"center": v(0, 0) * mm, "radius": 7.87 * mm});
            skCircle(sketch, "E45", {"center": v(0, 0) * mm, "radius": 4.9 * mm});
            skSolve(sketch);
        }
        {
            var Q0;
            Q0=makeQuery(id+"F14.imprint","IMPRINT",FACE,{"disambiguationData":[TD([[makeQuery(id+"F14.imprint","IMPRINT",EDGE,{"derivedFrom":sQuery(id+"F14.wireOp",EDGE,"E44")}),1.0]])]});
            var Q1;
            Q1=makeQuery(id+"F14.imprint","IMPRINT",FACE,{"disambiguationData":[TD([[makeQuery(id+"F14.imprint","IMPRINT",EDGE,{"derivedFrom":sQuery(id+"F14.wireOp",EDGE,"E45")}),1.0]])]});
            var Q2;
            Q2=makeQuery(id+"F8.opExtrude","CAP_FACE",FACE,{"disambiguationData":[OSD([sQuery(id+"F0.wireOp",EDGE,"E1"),sQuery(id+"F0.wireOp",EDGE,"E2"),sQuery(id+"F0.wireOp",EDGE,"E3"),sQuery(id+"F0.wireOp",EDGE,"E4"),sQuery(id+"F0.wireOp",EDGE,"E5.MirrorCS"),sQuery(id+"F0.wireOp",EDGE,"E6.MirrorCS"),sQuery(id+"F0.wireOp",EDGE,"E7.MirrorCS"),sQuery(id+"F0.wireOp",EDGE,"E8.MirrorCS"),sQuery(id+"F0.wireOp",EDGE,"E9.MirrorCS"),sQuery(id+"F0.wireOp",EDGE,"E10.MirrorCS"),sQuery(id+"F0.wireOp",EDGE,"E11.trimOffspring"),sQuery(id+"F0.wireOp",EDGE,"E12.trimOffspring"),sQuery(id+"F0.wireOp",EDGE,"E13.trimOffspring"),sQuery(id+"F0.wireOp",EDGE,"E14"),sQuery(id+"F0.wireOp",EDGE,"E15.MirrorCS"),sQuery(id+"F0.wireOp",EDGE,"E16.MirrorCS"),sQuery(id+"F0.wireOp",EDGE,"E17.MirrorCS")])],"isStart":false});
            extrude(context, id + "F15", {"entities" : qUnion([Q0, Q1]), "endBound" : BoundingType.UP_TO_SURFACE, "oppositeDirection" : true, "endBoundEntityFace" : qUnion([Q2]), "depth" : 25.4 * mm});
        }
        {
            var Q0;
            Q0 = qSketchRegion(id + "F14", true);
            extrude(context, id + "F16", {"entities" : qUnion([Q0]), "depth" : 0.25 * mm});
        }
        {
            var Q0;
            Q0=qCreatedBy(id+"F2.planeOp",FACE);
            var sketch = newSketch(context, id + "F17", { "sketchPlane" : qUnion([Q0])});
            skCircle(sketch, "E46", {"center": v(0, 0) * mm, "radius": 0.13 * mm});
            skSolve(sketch);
        }
        {
            var Q0;
            Q0=makeQuery(id+"F17.imprint","IMPRINT",FACE,{"disambiguationData":[TD([[makeQuery(id+"F17.imprint","IMPRINT",EDGE,{"derivedFrom":sQuery(id+"F17.wireOp",EDGE,"E46")}),1.0]])]});
            var Q1;
            Q1=sQuery(id+"F17.wireOp",EDGE,"E46");
            extrude(context, id + "F18", {"entities" : qUnion([Q0]), "surfaceEntities" : qUnion([Q1]), "depth" : 1.14 * mm});
        }
        {
            var Q0;
            Q0=qCreatedBy(id+"F2.planeOp",FACE);
            cPlane(context, id + "F19", {"entities" : qUnion([Q0]), "cplaneType" : CPlaneType.OFFSET, "offset" : 0.38 * mm, "width" : 152.4 * mm, "height" : 152.4 * mm});
        }
        {
            var Q0;
            Q0=qCreatedBy(id+"F19.planeOp",FACE);
            var sketch = newSketch(context, id + "F20", { "sketchPlane" : qUnion([Q0])});
            skArc(sketch, "E47", {"start": v(0.27, -0.03) * mm, "mid": v(-0.25, 0.1) * mm, "end": v(0.23, -0.15) * mm});
            skLineSegment(sketch, "E48", {"start": v(0, 0) * mm, "end": v(1.94, 0) * mm, "construction": true});
            skLineSegment(sketch, "E49", {"start": v(0, 0) * mm, "end": v(4.54, -1.65) * mm, "construction": true});
            skLineSegment(sketch, "E50", {"start": v(4.54, -1.65) * mm, "end": v(4.14, -1.22) * mm});
            skLineSegment(sketch, "E51", {"start": v(4.14, -1.22) * mm, "end": v(0.64, 0.05) * mm});
            skLineSegment(sketch, "E52", {"start": v(0.64, 0.05) * mm, "end": v(0.35, -0.07) * mm});
            skLineSegment(sketch, "E53", {"start": v(0.35, -0.07) * mm, "end": v(0.27, -0.03) * mm});
            skLineSegment(sketch, "E54.MirrorCS", {"start": v(0.45, -0.45) * mm, "end": v(0.31, -0.18) * mm});
            skLineSegment(sketch, "E55.MirrorCS", {"start": v(3.96, -1.73) * mm, "end": v(0.45, -0.45) * mm});
            skLineSegment(sketch, "E56.MirrorCS", {"start": v(4.54, -1.65) * mm, "end": v(3.96, -1.73) * mm});
            skLineSegment(sketch, "E57.MirrorCS", {"start": v(0.31, -0.18) * mm, "end": v(0.23, -0.15) * mm});
            skSolve(sketch);
        }
        {
            var Q0;
            Q0=qCreatedBy(id+"F19.planeOp",FACE);
            cPlane(context, id + "F21", {"entities" : qUnion([Q0]), "cplaneType" : CPlaneType.OFFSET, "offset" : 0.25 * mm, "width" : 152.4 * mm, "height" : 152.4 * mm});
        }
        {
            var Q0;
            Q0=qCreatedBy(id+"F21.planeOp",FACE);
            var sketch = newSketch(context, id + "F22", { "sketchPlane" : qUnion([Q0])});
            skArc(sketch, "E58", {"start": v(0.06, -0.26) * mm, "mid": v(0, 0.27) * mm, "end": v(-0.06, -0.26) * mm});
            skLineSegment(sketch, "E59", {"start": v(0, 0) * mm, "end": v(0, -6.14) * mm, "construction": true});
            skLineSegment(sketch, "E60", {"start": v(0, -6.14) * mm, "end": v(0.2, -5.58) * mm});
            skLineSegment(sketch, "E61", {"start": v(0.2, -5.58) * mm, "end": v(0.2, -0.5) * mm});
            skLineSegment(sketch, "E62", {"start": v(0.2, -0.5) * mm, "end": v(0.06, -0.35) * mm});
            skLineSegment(sketch, "E63", {"start": v(0.06, -0.35) * mm, "end": v(0.06, -0.26) * mm});
            skLineSegment(sketch, "E64.MirrorCS", {"start": v(-0.2, -0.5) * mm, "end": v(-0.06, -0.35) * mm});
            skLineSegment(sketch, "E65.MirrorCS", {"start": v(-0.2, -5.58) * mm, "end": v(-0.2, -0.5) * mm});
            skLineSegment(sketch, "E66.MirrorCS", {"start": v(0, -6.14) * mm, "end": v(-0.2, -5.58) * mm});
            skLineSegment(sketch, "E67.MirrorCS", {"start": v(-0.06, -0.35) * mm, "end": v(-0.06, -0.26) * mm});
            skSolve(sketch);
        }
        {
            var Q0;
            Q0 = qSketchRegion(id + "F20", true);
            var Q1;
            Q1 = qSketchRegion(id + "F22", true);
            extrude(context, id + "F23", {"entities" : qUnion([Q0, Q1]), "depth" : 0.15 * mm});
        }
        {
            var Q0;
            Q0=qCreatedBy(id+"F21.planeOp",FACE);
            cPlane(context, id + "F24", {"entities" : qUnion([Q0]), "cplaneType" : CPlaneType.OFFSET, "offset" : 0.2 * mm, "width" : 152.4 * mm, "height" : 152.4 * mm});
        }
        {
            var Q0;
            Q0=qCreatedBy(id+"F24.planeOp",FACE);
            var sketch = newSketch(context, id + "F25", { "sketchPlane" : qUnion([Q0])});
            skLineSegment(sketch, "E68", {"start": v(-5.12, 5.2) * mm, "end": v(0, 0) * mm, "construction": true});
            skLineSegment(sketch, "E69", {"start": v(-5.12, 5.2) * mm, "end": v(-5.07, 5.25) * mm});
            skLineSegment(sketch, "E70", {"start": v(-5.07, 5.25) * mm, "end": v(-0.1, 0.18) * mm});
            skLineSegment(sketch, "E71", {"start": v(1.75, -1.69) * mm, "end": v(1.7, -1.73) * mm});
            skLineSegment(sketch, "E72", {"start": v(0, 0) * mm, "end": v(1.7, -1.73) * mm, "construction": true});
            skLineSegment(sketch, "E73.MirrorCS", {"start": v(-5.16, 5.16) * mm, "end": v(-0.18, 0.1) * mm});
            skArc(sketch, "E74", {"start": v(0.18, -0.1) * mm, "mid": v(0.15, 0.14) * mm, "end": v(-0.1, 0.18) * mm});
            skLineSegment(sketch, "E75.trimOffspring", {"start": v(0.18, -0.1) * mm, "end": v(1.75, -1.69) * mm});
            skArc(sketch, "E76.trimOffspring", {"start": v(-0.18, 0.1) * mm, "mid": v(-0.15, -0.14) * mm, "end": v(0.1, -0.18) * mm});
            skLineSegment(sketch, "E77.trimOffspring", {"start": v(0.1, -0.18) * mm, "end": v(1.66, -1.77) * mm});
            skCircle(sketch, "E78.0", {"center": v(0, 0) * mm, "radius": 0.13 * mm});
            skLineSegment(sketch, "E79", {"start": v(1.66, -1.77) * mm, "end": v(1.7, -1.73) * mm});
            skLineSegment(sketch, "E80", {"start": v(-5.16, 5.16) * mm, "end": v(-5.12, 5.2) * mm});
            skSolve(sketch);
        }
        {
            var Q0;
            Q0 = qSketchRegion(id + "F25", true);
            extrude(context, id + "F26", {"entities" : qUnion([Q0]), "depth" : 0.08 * mm});
        }
        {
            var Q0;
            Q0=qCreatedBy(id+"F2.planeOp",FACE);
            var sketch = newSketch(context, id + "F27", { "sketchPlane" : qUnion([Q0])});
            skText(sketch, "E81", { "text": "FOSSIL", "fontName": "OpenSans-Bold.ttf"});
            const initialGuessF27  = {"E81": [-0.00152, 0.00299, 1, 0, 0.00065]};
            skSetInitialGuess(sketch, initialGuessF27);
            skSolve(sketch);
        }
        {
            var Q0;
            Q0 = qSketchRegion(id + "F27", true);
            extrude(context, id + "F28", {"entities" : qUnion([Q0]), "depth" : 0.03 * mm});
        }
        {
            var Q0;
            Q0=qCreatedBy(makeId("Right.planeOp"),FACE);
            var sketch = newSketch(context, id + "F29", { "sketchPlane" : qUnion([Q0])});
            skLineSegment(sketch, "E82", {"start": v(-9.53, 0) * mm, "end": v(-13.14, -3.6) * mm});
            skLineSegment(sketch, "E83.0", {"start": v(-13.14, -3.6) * mm, "end": v(-13.14, 0) * mm});
            skLineSegment(sketch, "E84", {"start": v(-13.14, 0) * mm, "end": v(-9.53, 0) * mm});
            skSolve(sketch);
        }
        {
            var Q0;
            Q0 = qSketchRegion(id + "F29", true);
            var Q1;
            Q1=makeQuery(id+"F1.opExtrude","SWEPT_FACE",FACE,{"disambiguationData":[OSD([sQuery(id+"F0.wireOp",EDGE,"E6.MirrorCS")])]});
            var Q2;
            Q2=makeQuery(id+"F1.opExtrude","SWEPT_FACE",FACE,{"disambiguationData":[OSD([sQuery(id+"F0.wireOp",EDGE,"E9.MirrorCS")])]});
            extrude(context, id + "F30", {"entities" : qUnion([Q0]), "operationType" : NewBodyOperationType.REMOVE, "endBound" : BoundingType.UP_TO_SURFACE, "endBoundEntityFace" : qUnion([Q1]), "depth" : 25.4 * mm, "hasSecondDirection" : true, "secondDirectionBound" : SecondDirectionBoundingType.UP_TO_SURFACE, "secondDirectionOppositeDirection" : true, "secondDirectionBoundEntityFace" : qUnion([Q2]), "secondDirectionDepth" : 25.4 * mm});
        }
    });
